# Revit family: Gira_004600rfa
name_source: partatom
category: Allgemeines Modell
revit_build: Autodesk Revit 2017 (Build: 20160225_1515(x64)
units: mm (PartAtom-declared; Revit-internal decimal feet)

## family parameters
Basisbauteil = Fläche
Beim Laden mit Abzugskörper schneiden = Nein
Bemaßung runder Anschluss = Durchmesser verwenden
Gemeinsam genutzt = Nein
Kann Basisbauteil für Bewehrung sein = Nein
Raumberechnungspunkt = Nein
Teiletyp = Normal

## types (1)
- Gira_004600rfa
    Assembly arrangement = Basic element
    BIM = https://media.stage.bim.site
    Beschreibung = Aerial sock.EDU 04 F Ins.,Antenna socket insert (EDU 04 F),,,Features:,- Can be used as a single box.,- The entire signal spectrum from 4 to 2400 MHz is available on both connections.,- Via the TV connection, transferring direct current (max. DC 24 V   500 mA) to a satellite antenna is possible.,,Notes :,- For screw mounting only.,- Important! Observe construction space for plug and bending radii.,- If using with gender changers:,  Not suitable for duct installation or a standard device box.,  Connection with angled plug recommended.,- Installation recommendation:,  Kaiser electronic outlets,  flush-mounted installation: Kaiser Order No.: 1068-02,  hollow-wall installation: Kaiser Order No.: 9062-94,  concrete installation: Kaiser Order No.: 1268-40,- For use in individual antenna systems and for communal antenna systems, area couplers, and satellite house distribution systems on decoupled branch lines.
    Category = Other
    Colour = Other
    Connection type = Screw
    Data sheet = https://katalog.gira.de
    Degree of protection (IP) = IP20
    Frequency [Hz] = [4000000:2400000000]
    GTIN = 4010337046004
    HAN = 004600
    Halogen free = Nein
    Hersteller = Gira
    Integrated timer = Nein
    Material = Other
    Material quality = Other
    Max. switching power [Voltampere] = 1000
    Mechanical coding = Nein
    Model = Loop-through socket
    Mounting method = Flush mounted (plaster)
    Mounting method shielding connection = Screw
    Nominal voltage [Volt] = 230
    Productwebsite = http://katalog.gira.de
    Random generator = Nein
    Separate strain relief = Ja
    Shielded buses = Ja
    Shielded housing = Nein
    Substation input = Ja
    Suitable for degree of protection (IP) = IP20
    Suitable for rain sensor = Nein
    Suitable for wind sensor = Nein
    Surface finishing = Not applicable
    Surface protection = Other
    Switch-off protection = Nein
    Through loss at 2150 MHz [B] = 0.1
    Through loss at 860 MHz [B] = 0.1
    Transparent = Nein
    Type of fastening = Screwing
    Typname = Antenna sock. EDU 04 F Insert
    URL = https://www.gira.de
    Vorgabe-Ansicht = 1219 mm
    With Astro program = Nein
    With brightness sensor connection = Nein
    With glass breaking detector connection = Nein
    With memory function = Nein

## geometry (parser evidence)
native form markers: Sweep x2
no freeform markers — native parametric forms only
